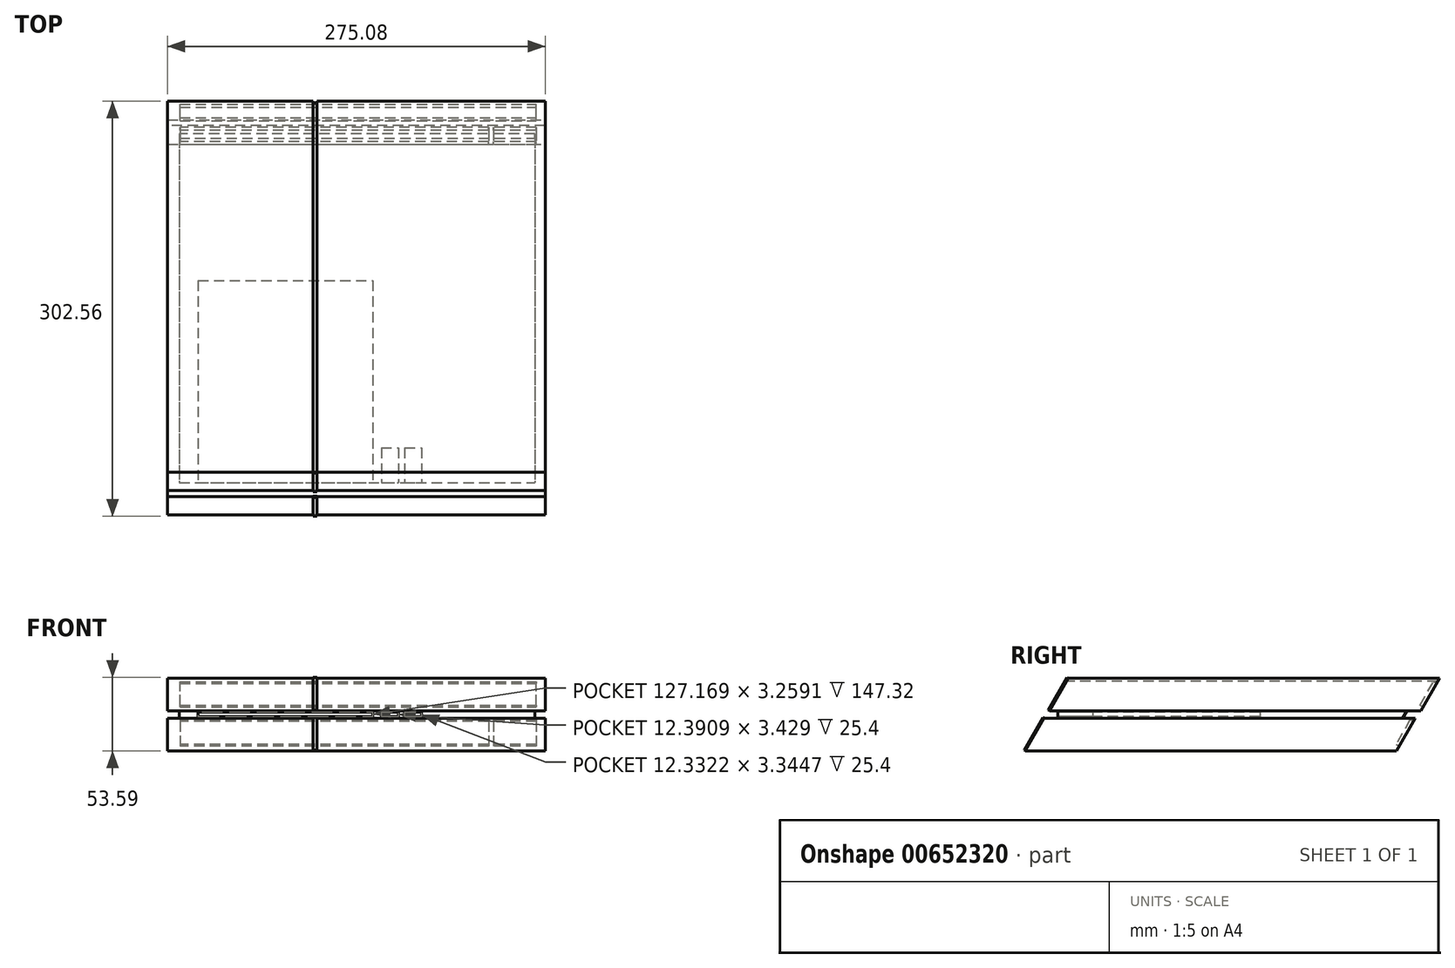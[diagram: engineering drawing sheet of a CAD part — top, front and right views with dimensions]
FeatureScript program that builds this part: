
annotation { "Feature Type Name" : "Feature", "Feature Type Description" : "" }
export const myFeature = defineFeature(function(context is Context, id is Id, definition is map)
    precondition{}
    {
        {
            var Q0;
            Q0=qCreatedBy(makeId("Top.planeOp"),FACE);
            var sketch = newSketch(context, id + "F0", { "sketchPlane" : qUnion([Q0])});
            skLineSegment(sketch, "E0.bottom", {"start": v(-137.54, 152.53) * mm, "end": v(137.54, 152.53) * mm});
            skLineSegment(sketch, "E0.top", {"start": v(-137.54, -152.53) * mm, "end": v(137.54, -152.53) * mm});
            skLineSegment(sketch, "E0.left", {"start": v(-137.54, 152.53) * mm, "end": v(-137.54, -152.53) * mm});
            skLineSegment(sketch, "E0.right", {"start": v(137.54, 152.53) * mm, "end": v(137.54, -152.53) * mm});
            skPoint(sketch, "E0.middle", {"position": v(0, 0) * mm});
            skSolve(sketch);
        }
        {
            var Q0;
            Q0 = qSketchRegion(id + "F0", true);
            extrude(context, id + "F1", {"entities" : qUnion([Q0]), "depth" : 23.88 * mm, "offsetDistance" : 25.4 * mm});
        }
        {
            var Q0;
            Q0=makeQuery(id+"F1.opExtrude","CAP_EDGE",EDGE,{"disambiguationData":[OSD([sQuery(id+"F0.wireOp",EDGE,"E0.top")])],"isStart":false});
            chamfer(context, id + "F2", {"entities" : qUnion([Q0]), "chamferType" : ChamferType.OFFSET_ANGLE, "width" : 24.13 * mm, "oppositeDirection" : false, "angle" : 60.33 * degree, "tangentPropagation" : true});
        }
        {
            var Q0;
            Q0=makeQuery(id+"F1.opExtrude","CAP_EDGE",EDGE,{"disambiguationData":[OSD([sQuery(id+"F0.wireOp",EDGE,"E0.bottom")])],"isStart":true});
            chamfer(context, id + "F3", {"entities" : qUnion([Q0]), "chamferType" : ChamferType.OFFSET_ANGLE, "width" : 24.13 * mm, "oppositeDirection" : false, "angle" : 60.33 * degree, "tangentPropagation" : true});
        }
        {
            var Q0;
            Q0=makeQuery(id+"F1.opExtrude","CAP_FACE",FACE,{"disambiguationData":[OSD([sQuery(id+"F0.wireOp",EDGE,"E0.bottom"),sQuery(id+"F0.wireOp",EDGE,"E0.top"),sQuery(id+"F0.wireOp",EDGE,"E0.left"),sQuery(id+"F0.wireOp",EDGE,"E0.right")])],"isStart":false});
            var sketch = newSketch(context, id + "F4", { "sketchPlane" : qUnion([Q0])});
            skLineSegment(sketch, "E1.bottom", {"start": v(-129.05, 135.9) * mm, "end": v(130.03, 135.9) * mm});
            skLineSegment(sketch, "E1.top", {"start": v(-129.05, -118.35) * mm, "end": v(130.03, -118.35) * mm});
            skLineSegment(sketch, "E1.left", {"start": v(-129.05, 135.9) * mm, "end": v(-129.05, -118.35) * mm});
            skLineSegment(sketch, "E1.right", {"start": v(130.03, 135.9) * mm, "end": v(130.03, -118.35) * mm});
            skSolve(sketch);
        }
        {
            var Q0;
            Q0 = qSketchRegion(id + "F4", true);
            extrude(context, id + "F5", {"entities" : qUnion([Q0]), "depth" : 5.33 * mm, "offsetDistance" : 25.4 * mm});
        }
        {
            var Q0;
            Q0=makeQuery(id+"F1.opExtrude","SWEPT_BODY",BODY,{"disambiguationData":[OSD([sQuery(id+"F0.wireOp",EDGE,"E0.bottom"),sQuery(id+"F0.wireOp",EDGE,"E0.top"),sQuery(id+"F0.wireOp",EDGE,"E0.left"),sQuery(id+"F0.wireOp",EDGE,"E0.right")])]});
            transform(context, id + "F6", {"entities" : qUnion([Q0]), "transformType" : TransformType.TRANSLATION_3D, "dx" : 0 * mm, "dy" : 17.78 * mm, "dz" : 29.2 * mm, "makeCopy" : true});
        }
        {
            var Q0;
            Q0=makeQuery(id+"F6.opPattern","COPY",FACE,{"derivedFrom":makeQuery(id+"F3.opChamfer","BLEND_FACE",FACE,{"disambiguationData":[OSD([sQuery(id+"F0.wireOp",EDGE,"E0.bottom")])]}),"instanceName":"1"});
            var sketch = newSketch(context, id + "F7", { "sketchPlane" : qUnion([Q0])});
            skLineSegment(sketch, "E2.bottom", {"start": v(128.5, 101.05) * mm, "end": v(-131.1, 101.05) * mm});
            skLineSegment(sketch, "E2.top", {"start": v(128.5, 120.6) * mm, "end": v(-131.1, 120.6) * mm});
            skLineSegment(sketch, "E2.left", {"start": v(128.5, 101.05) * mm, "end": v(128.5, 120.6) * mm});
            skLineSegment(sketch, "E2.right", {"start": v(-131.1, 101.05) * mm, "end": v(-131.1, 120.6) * mm});
            skSolve(sketch);
        }
        {
            var Q0;
            Q0 = qSketchRegion(id + "F7", true);
            extrude(context, id + "F8", {"entities" : qUnion([Q0]), "operationType" : NewBodyOperationType.REMOVE, "oppositeDirection" : true, "depth" : 2.54 * mm, "offsetDistance" : 25.4 * mm});
        }
        {
            var Q0;
            Q0=makeQuery(id+"F3.opChamfer","BLEND_FACE",FACE,{"disambiguationData":[OSD([sQuery(id+"F0.wireOp",EDGE,"E0.bottom")])]});
            var sketch = newSketch(context, id + "F9", { "sketchPlane" : qUnion([Q0])});
            skLineSegment(sketch, "E3.bottom", {"start": v(-131.1, 88.23) * mm, "end": v(-100.01, 88.23) * mm});
            skLineSegment(sketch, "E3.top", {"start": v(-131.1, 67.37) * mm, "end": v(-100.01, 67.37) * mm});
            skLineSegment(sketch, "E3.left", {"start": v(-131.1, 88.23) * mm, "end": v(-131.1, 67.37) * mm});
            skLineSegment(sketch, "E3.right", {"start": v(-100.01, 88.23) * mm, "end": v(-100.01, 67.37) * mm});
            skPoint(sketch, "E4.oppositeSnap0", {"position": v(-115.55, 67.37) * mm});
            skLineSegment(sketch, "E4.bottom", {"start": v(-96.27, 88.23) * mm, "end": v(128.5, 88.23) * mm});
            skLineSegment(sketch, "E4.top", {"start": v(-96.27, 67.37) * mm, "end": v(128.5, 67.37) * mm});
            skLineSegment(sketch, "E4.left", {"start": v(-96.27, 88.23) * mm, "end": v(-96.27, 67.37) * mm});
            skLineSegment(sketch, "E4.right", {"start": v(128.5, 88.23) * mm, "end": v(128.5, 67.37) * mm});
            skSolve(sketch);
        }
        {
            var Q0;
            Q0 = qSketchRegion(id + "F9", true);
            extrude(context, id + "F10", {"entities" : qUnion([Q0]), "operationType" : NewBodyOperationType.REMOVE, "oppositeDirection" : true, "depth" : 2.54 * mm, "offsetDistance" : 25.4 * mm});
        }
        {
            var Q0;
            Q0=makeQuery(id+"F6.opPattern","COPY",FACE,{"derivedFrom":makeQuery(id+"F1.opExtrude","CAP_FACE",FACE,{"disambiguationData":[OSD([sQuery(id+"F0.wireOp",EDGE,"E0.bottom"),sQuery(id+"F0.wireOp",EDGE,"E0.top"),sQuery(id+"F0.wireOp",EDGE,"E0.left"),sQuery(id+"F0.wireOp",EDGE,"E0.right")])],"isStart":false}),"instanceName":"1"});
            var sketch = newSketch(context, id + "F11", { "sketchPlane" : qUnion([Q0])});
            skLineSegment(sketch, "E5.bottom", {"start": v(-137.54, 159.78) * mm, "end": v(-31.7, 159.78) * mm});
            skLineSegment(sketch, "E5.top", {"start": v(-137.54, -110.62) * mm, "end": v(-31.7, -110.62) * mm});
            skLineSegment(sketch, "E5.left", {"start": v(-137.54, 159.78) * mm, "end": v(-137.54, -110.62) * mm});
            skLineSegment(sketch, "E5.right", {"start": v(-31.7, 159.78) * mm, "end": v(-31.7, -110.62) * mm});
            skSolve(sketch);
        }
        {
            var Q0;
            {var subQ0=sQuery(id+"F11.wireOp",EDGE,"E5.right");Q0=makeQuery(id+"F11.imprint","IMPRINT",FACE,{"disambiguationData":[TD([[makeQuery(id+"F11.imprint","IMPRINT",EDGE,{"derivedFrom":subQ0}),1.0]])]});}
            var sketch = newSketch(context, id + "F12", { "sketchPlane" : qUnion([Q0])});
            skLineSegment(sketch, "E6.bottom", {"start": v(-28.64, 161.76) * mm, "end": v(-31.64, 161.76) * mm});
            skLineSegment(sketch, "E6.top", {"start": v(-28.64, -112.56) * mm, "end": v(-31.64, -112.56) * mm});
            skLineSegment(sketch, "E6.left", {"start": v(-28.64, 161.76) * mm, "end": v(-28.64, -112.56) * mm});
            skLineSegment(sketch, "E6.right", {"start": v(-31.64, 161.76) * mm, "end": v(-31.64, -112.56) * mm});
            skSolve(sketch);
        }
        {
            var Q0;
            Q0 = qSketchRegion(id + "F12", true);
            extrude(context, id + "F13", {"entities" : qUnion([Q0]), "operationType" : NewBodyOperationType.REMOVE, "oppositeDirection" : true, "depth" : 2.3 * mm, "offsetDistance" : 25.4 * mm});
        }
        {
            var Q0;
            Q0=makeQuery(id+"F6.opPattern","COPY",FACE,{"derivedFrom":makeQuery(id+"F2.opChamfer","BLEND_FACE",FACE,{"disambiguationData":[OSD([sQuery(id+"F0.wireOp",EDGE,"E0.top")])]}),"instanceName":"1"});
            var sketch = newSketch(context, id + "F14", { "sketchPlane" : qUnion([Q0])});
            skLineSegment(sketch, "E7.bottom", {"start": v(-31.64, -8.63) * mm, "end": v(-28.64, -8.63) * mm});
            skLineSegment(sketch, "E7.top", {"start": v(-31.64, -36.1) * mm, "end": v(-28.64, -36.1) * mm});
            skLineSegment(sketch, "E7.left", {"start": v(-31.64, -8.63) * mm, "end": v(-31.64, -36.1) * mm});
            skLineSegment(sketch, "E7.right", {"start": v(-28.64, -8.63) * mm, "end": v(-28.64, -36.1) * mm});
            skSolve(sketch);
        }
        {
            var Q0;
            Q0 = qSketchRegion(id + "F14", true);
            extrude(context, id + "F15", {"entities" : qUnion([Q0]), "depth" : 1.02 * mm, "offsetDistance" : 25.4 * mm});
        }
        {
            var Q0;
            Q0=makeQuery(id+"F15.opExtrude","SWEPT_BODY",BODY,{"disambiguationData":[OSD([sQuery(id+"F14.wireOp",EDGE,"E7.bottom"),sQuery(id+"F14.wireOp",EDGE,"E7.top"),sQuery(id+"F14.wireOp",EDGE,"E7.left"),sQuery(id+"F14.wireOp",EDGE,"E7.right")])]});
            transform(context, id + "F16", {"entities" : qUnion([Q0]), "transformType" : TransformType.TRANSLATION_3D, "dx" : 0 * mm, "dy" : -17.68 * mm, "dz" : -29.08 * mm, "makeCopy" : true});
        }
        {
            var Q0;
            Q0=makeQuery(id+"F5.opExtrude","SWEPT_FACE",FACE,{"disambiguationData":[OSD([sQuery(id+"F4.wireOp",EDGE,"E1.top")])]});
            var sketch = newSketch(context, id + "F17", { "sketchPlane" : qUnion([Q0])});
            skLineSegment(sketch, "E8.bottom", {"start": v(-115.25, 28.17) * mm, "end": v(11.92, 28.17) * mm});
            skLineSegment(sketch, "E8.top", {"start": v(-115.25, 24.91) * mm, "end": v(11.92, 24.91) * mm});
            skLineSegment(sketch, "E8.left", {"start": v(-115.25, 28.17) * mm, "end": v(-115.25, 24.91) * mm});
            skLineSegment(sketch, "E8.right", {"start": v(11.92, 28.17) * mm, "end": v(11.92, 24.91) * mm});
            skSolve(sketch);
        }
        {
            var Q0;
            Q0 = qSketchRegion(id + "F17", true);
            extrude(context, id + "F18", {"entities" : qUnion([Q0]), "operationType" : NewBodyOperationType.REMOVE, "oppositeDirection" : true, "depth" : 147.32 * mm, "offsetDistance" : 25.4 * mm});
        }
        {
            var Q0;
            Q0=makeQuery(id+"F5.opExtrude","SWEPT_FACE",FACE,{"disambiguationData":[OSD([sQuery(id+"F4.wireOp",EDGE,"E1.top")])]});
            var sketch = newSketch(context, id + "F19", { "sketchPlane" : qUnion([Q0])});
            skLineSegment(sketch, "E9.bottom", {"start": v(18.18, 28.3) * mm, "end": v(30.57, 28.3) * mm});
            skLineSegment(sketch, "E9.top", {"start": v(18.18, 24.87) * mm, "end": v(30.57, 24.87) * mm});
            skLineSegment(sketch, "E9.left", {"start": v(18.18, 28.3) * mm, "end": v(18.18, 24.87) * mm});
            skLineSegment(sketch, "E9.right", {"start": v(30.57, 28.3) * mm, "end": v(30.57, 24.87) * mm});
            skSolve(sketch);
        }
        {
            var Q0;
            Q0=makeQuery(id+"F19.imprint","IMPRINT",FACE,{"disambiguationData":[TD([[makeQuery(id+"F19.imprint","IMPRINT",EDGE,{"derivedFrom":sQuery(id+"F19.wireOp",EDGE,"E9.bottom")}),-1.0]])]});
            extrude(context, id + "F20", {"entities" : qUnion([Q0]), "operationType" : NewBodyOperationType.REMOVE, "oppositeDirection" : true, "depth" : 25.4 * mm, "offsetDistance" : 25.4 * mm});
        }
        {
            var Q0;
            Q0=makeQuery(id+"F5.opExtrude","SWEPT_FACE",FACE,{"disambiguationData":[OSD([sQuery(id+"F4.wireOp",EDGE,"E1.top")])]});
            var sketch = newSketch(context, id + "F21", { "sketchPlane" : qUnion([Q0])});
            skLineSegment(sketch, "E10.bottom", {"start": v(35.26, 28.26) * mm, "end": v(47.6, 28.26) * mm});
            skLineSegment(sketch, "E10.top", {"start": v(35.26, 24.91) * mm, "end": v(47.6, 24.91) * mm});
            skLineSegment(sketch, "E10.left", {"start": v(35.26, 28.26) * mm, "end": v(35.26, 24.91) * mm});
            skLineSegment(sketch, "E10.right", {"start": v(47.6, 28.26) * mm, "end": v(47.6, 24.91) * mm});
            skSolve(sketch);
        }
        {
            var Q0;
            Q0 = qSketchRegion(id + "F21", true);
            extrude(context, id + "F22", {"entities" : qUnion([Q0]), "operationType" : NewBodyOperationType.REMOVE, "oppositeDirection" : true, "depth" : 25.4 * mm, "offsetDistance" : 25.4 * mm});
        }
        {
            var Q0;
            Q0=makeQuery(id+"F5.opExtrude","CAP_EDGE",EDGE,{"disambiguationData":[OSD([sQuery(id+"F4.wireOp",EDGE,"E1.bottom")])],"isStart":true});
            chamfer(context, id + "F23", {"entities" : qUnion([Q0]), "chamferType" : ChamferType.OFFSET_ANGLE, "width" : 3.05 * mm, "oppositeDirection" : false, "angle" : 60.33 * degree, "tangentPropagation" : true});
        }
    });
